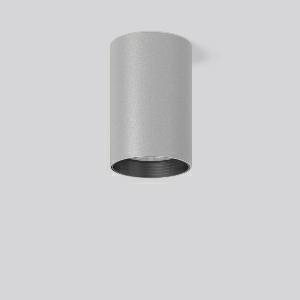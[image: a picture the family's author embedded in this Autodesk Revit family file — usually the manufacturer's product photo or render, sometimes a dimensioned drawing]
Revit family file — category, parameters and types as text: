
# Revit family: heledon_maxi_a_931220_004_2_351d
name_source: partatom
category: Lighting Fixtures
units: mm (PartAtom-declared; Revit-internal decimal feet)

## family parameters
Cut with Voids When Loaded = No
Host = Face
Light Source = No
Part Type = Normal
Room Calculation Point = No
Round Connector Dimension = Use Diameter
Shared = No

## types (1)
- HELEDON maxi A (1 x LED Modul 927, 2650 lm, 2700)
    Apparent Load = 25 VA
    Approval mark = CE
    CIE Flux Codes = 97 100 100 100 100
    Color Rendering = 92
    Color Temperature = 2700
    Default Elevation = 1800 mm
    Description = Series: HELEDON maxi
Cylindrical surface-mounted downlight. Housing: die-cast aluminium, powder-coated. Internal ceiling frame polycarbonate with bayonet mounting. Black plastic ring and recessed LED to prevent glare from the side. Optical assembly with lens made of plastic (polycarbonate) for the best homogeneous light distribution - can be changed without tools. Best colour rendering index Ra>90. Suitable for Ceiling mounting. Easy installation with a separate ceiling frame with bayonet mounting and plug connection. Driver integrated. Connected via plug-in connector. High quality converter without flickering and stroboscopic effect. The following accessories can be mounted without use of tools: interchangeable lenses, decorative glasses, honeycomb louvre, clear and frosted diffusers, white interchangeable plastic ring. 
Colour: silver
Diameter: 123 mm
Height: 183 mm
Lamp: LED
Socket: without socket
Colour temperature: 2700K
Colour rendering index (CRI): 92
System power: 25 W
Rated luminous flux: 2650 lm
Luminous efficiency: 106 lm/W
Control gear: Regulated power supply
Protection class: I
Type of protection: IP 20
    Height = 183 mm
    Lamp = 1 x LED Modul 927
    Lamp Light Flux = 2650 lm
    Lamp count = 1
    Length = 123 mm
    Lifetime = 50000 h
    Luminous efficacy = 106 lm/W
    Manufacturer = RZB
    ModVariant = No
    Model = 931220.004.2
    Mounting Place = Ceiling
    Mounting Type = Surface mounted
    Number of Poles = 1
    OnlyDefault = Yes
    Power Factor = 1
    Product Name = HELEDON maxi A
    Product group = Surface mounted downlights
    ProductGroupID = 302
    Protection Class = Protection class I
    Protection Degree = IP 20
    RLX_Detail_Level = 1
    RLX_Emergency_Light_Flux = 0 lm
    RLX_Emergency_Type = 0
    RLX_Emergency_Type_DB = No
    RlxData = <blob elided: 100049 chars, md5=b0cf871f>
    Socket = socket
    Standby Power = 0 W
    System Light Flux = 2650 lm
    System Power = 25 W
    Type Comments = Product without accessories
    Type Image = 931193.004.jpg
    URL = http://relux.com
    VarID = ---
    Voltage = 230 V
    Voltage Range = 220-240 V
    Weight = 0.00 kg
    Width = 0 mm  [stored 0 ft]

note: [stored X ft] marks values corroborated as IEEE doubles in the binary element streams (Revit-internal decimal feet)

## geometry (parser evidence)
native form markers: Blend x4, Sweep x10
no freeform markers — native parametric forms only
